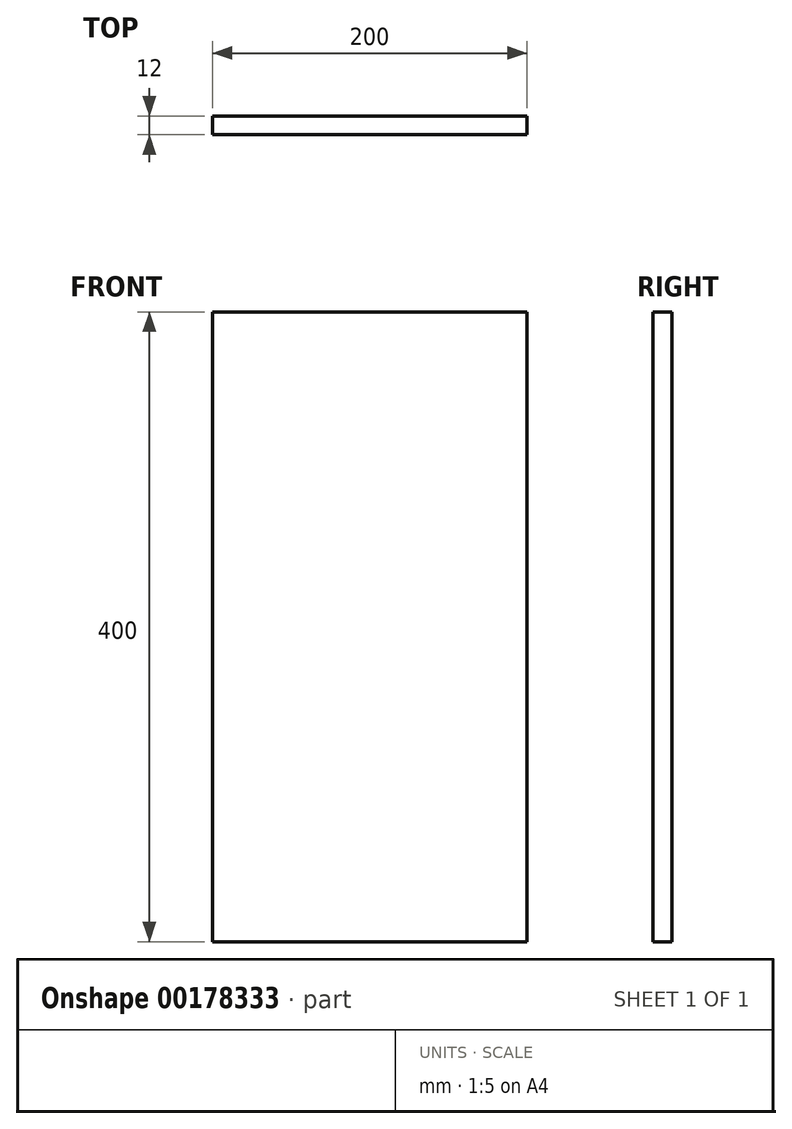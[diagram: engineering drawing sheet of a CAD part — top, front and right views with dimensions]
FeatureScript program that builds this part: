
annotation { "Feature Type Name" : "Feature", "Feature Type Description" : "" }
export const myFeature = defineFeature(function(context is Context, id is Id, definition is map)
    precondition{}
    {
        {
            var Q0;
            Q0=qCreatedBy(makeId("Front.planeOp"),FACE);
            var sketch = newSketch(context, id + "F0", { "sketchPlane" : qUnion([Q0])});
            skLineSegment(sketch, "E0", {"start": v(0, 0) * mm, "end": v(200, 0) * mm});
            skLineSegment(sketch, "E1", {"start": v(200, 0) * mm, "end": v(200, 400) * mm});
            skLineSegment(sketch, "E2", {"start": v(0, 0) * mm, "end": v(0, 400) * mm});
            skLineSegment(sketch, "E3", {"start": v(0, 400) * mm, "end": v(200, 400) * mm});
            skSolve(sketch);
        }
        {
            var Q0;
            Q0=makeQuery(id+"F0.imprint","IMPRINT",FACE,{"disambiguationData":[TD([[makeQuery(id+"F0.imprint","IMPRINT",EDGE,{"derivedFrom":sQuery(id+"F0.wireOp",EDGE,"E0")}),1.0]])]});
            extrude(context, id + "F1", {"entities" : qUnion([Q0]), "depth" : 12 * mm, "offsetDistance" : 25 * mm});
        }
    });
